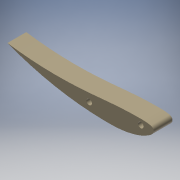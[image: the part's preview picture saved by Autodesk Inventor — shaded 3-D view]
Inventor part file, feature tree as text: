
AUTODESK INVENTOR PART (.ipt)
format: ipt  version: 2018 (Build 220112000, 112)  size: 122,880 bytes
history: native  units: mm
features: extrude x1, sketch x1, projected_geometry x1
ambient origin geometry x8: Origin, YZ Plane, XZ Plane, XY Plane, X Axis, Y Axis, Z Axis, Center Point
bodies: Body1 (feature_tree)
feature tree (3):
  extrude  "押し出し2"  Depth=40.2mm TaperAngle=0.0deg
  sketch  "スケッチ1"
  projected_geometry  "投影ループ1"
